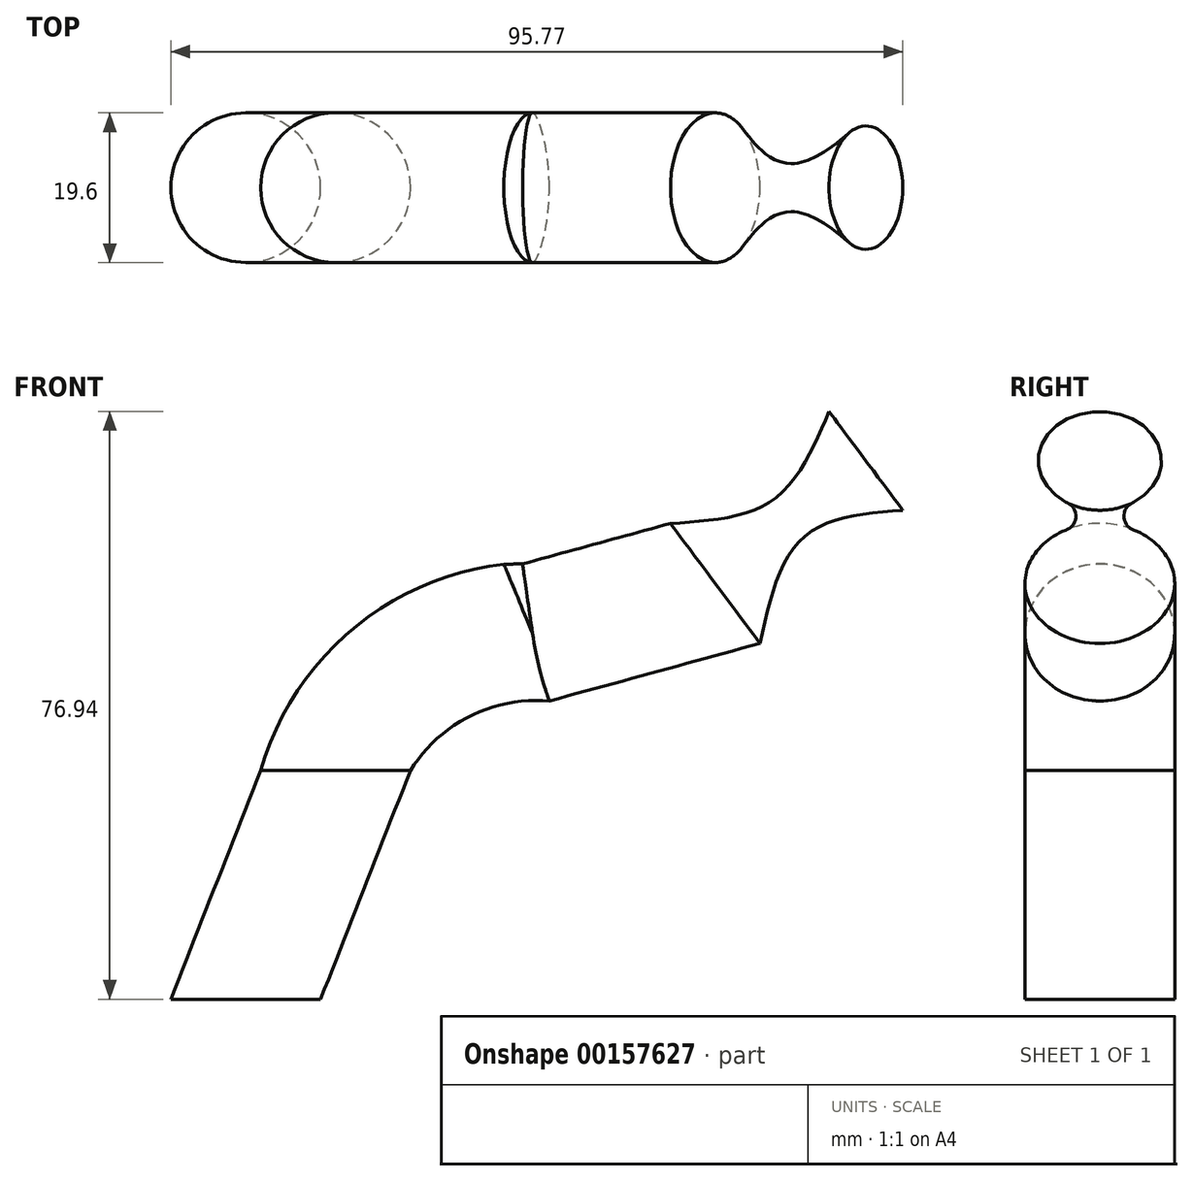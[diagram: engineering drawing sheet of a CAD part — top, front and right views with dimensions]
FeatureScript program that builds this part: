
annotation { "Feature Type Name" : "Feature", "Feature Type Description" : "" }
export const myFeature = defineFeature(function(context is Context, id is Id, definition is map)
    precondition{}
    {
        {
            var Q0;
            Q0=qCreatedBy(makeId("Front.planeOp"),FACE);
            var sketch = newSketch(context, id + "F0", { "sketchPlane" : qUnion([Q0])});
            skLineSegment(sketch, "E0", {"start": v(0, 0) * mm, "end": v(11.76, 29.97) * mm});
            skArc(sketch, "E1", {"start": v(37.53, 47.9) * mm, "mid": v(21.93, 42.84) * mm, "end": v(11.76, 29.97) * mm});
            skLineSegment(sketch, "E2", {"start": v(37.53, 47.9) * mm, "end": v(61.43, 54.43) * mm});
            skSolve(sketch);
        }
        {
            var Q0;
            Q0=qCreatedBy(makeId("Top.planeOp"),FACE);
            var sketch = newSketch(context, id + "F1", { "sketchPlane" : qUnion([Q0])});
            skCircle(sketch, "E3", {"center": v(0, 0) * mm, "radius": 9.8 * mm});
            skSolve(sketch);
        }
        {
            var Q0;
            Q0=makeQuery(id+"F1.imprint","IMPRINT",FACE,{"disambiguationData":[TD([[makeQuery(id+"F1.imprint","IMPRINT",EDGE,{"derivedFrom":sQuery(id+"F1.wireOp",EDGE,"E3")}),1.0]])]});
            var Q1;
            Q1=sQuery(id+"F0.wireOp",EDGE,"E0");
            var Q2;
            Q2=sQuery(id+"F0.wireOp",EDGE,"E1");
            var Q3;
            Q3=sQuery(id+"F0.wireOp",EDGE,"E2");
            sweep(context, id + "F2", {"profiles" : qUnion([Q0]), "path" : qUnion([Q1, Q2, Q3])});
        }
        {
            var Q0;
            Q0=makeQuery(id+"F2.opSweep","CAP_FACE",FACE,{"disambiguationData":[OSD([sQuery(id+"F0.wireOp",VERTEX,"E2.end"),sQuery(id+"F1.wireOp",EDGE,"E3")])],"isStart":false});
            cPlane(context, id + "F3", {"entities" : qUnion([Q0]), "cplaneType" : CPlaneType.OFFSET, "offset" : 25.4 * mm, "width" : 152.4 * mm, "height" : 152.4 * mm});
        }
        {
            var Q0;
            Q0=qCreatedBy(id+"F3.planeOp",FACE);
            var sketch = newSketch(context, id + "F4", { "sketchPlane" : qUnion([Q0])});
            skCircle(sketch, "E4", {"center": v(0, 7.97) * mm, "radius": 8.07 * mm});
            skSolve(sketch);
        }
        {
            var Q0;
            Q0=makeQuery(id+"F2.opSweep","CAP_FACE",FACE,{"disambiguationData":[OSD([sQuery(id+"F0.wireOp",VERTEX,"E2.end"),sQuery(id+"F1.wireOp",EDGE,"E3")])],"isStart":false});
            cPlane(context, id + "F5", {"entities" : qUnion([Q0]), "cplaneType" : CPlaneType.OFFSET, "offset" : 12.7 * mm, "width" : 152.4 * mm, "height" : 152.4 * mm});
        }
        {
            var Q0;
            Q0=qCreatedBy(id+"F5.planeOp",FACE);
            var sketch = newSketch(context, id + "F6", { "sketchPlane" : qUnion([Q0])});
            skCircle(sketch, "E5", {"center": v(0, 7.97) * mm, "radius": 3.16 * mm});
            skSolve(sketch);
        }
        {
            var Q1;
            Q1=makeQuery(id+"F2.opSweep","CAP_FACE",FACE,{"disambiguationData":[OSD([sQuery(id+"F0.wireOp",VERTEX,"E2.end"),sQuery(id+"F1.wireOp",EDGE,"E3")])],"isStart":false});
            var Q2;
            Q2=makeQuery(id+"F6.imprint","IMPRINT",FACE,{"disambiguationData":[TD([[makeQuery(id+"F6.imprint","IMPRINT",EDGE,{"derivedFrom":sQuery(id+"F6.wireOp",EDGE,"E5")}),1.0]])]});
            var Q3;
            Q3=makeQuery(id+"F4.imprint","IMPRINT",FACE,{"disambiguationData":[TD([[makeQuery(id+"F4.imprint","IMPRINT",EDGE,{"derivedFrom":sQuery(id+"F4.wireOp",EDGE,"E4")}),1.0]])]});
            loft(context, id + "F7", {"operationType" : NewBodyOperationType.ADD, "sheetProfilesArray" : [{ "sheetProfileEntities" : qUnion([Q1]) }, { "sheetProfileEntities" : qUnion([Q2]) }, { "sheetProfileEntities" : qUnion([Q3]) }]});
        }
    });
